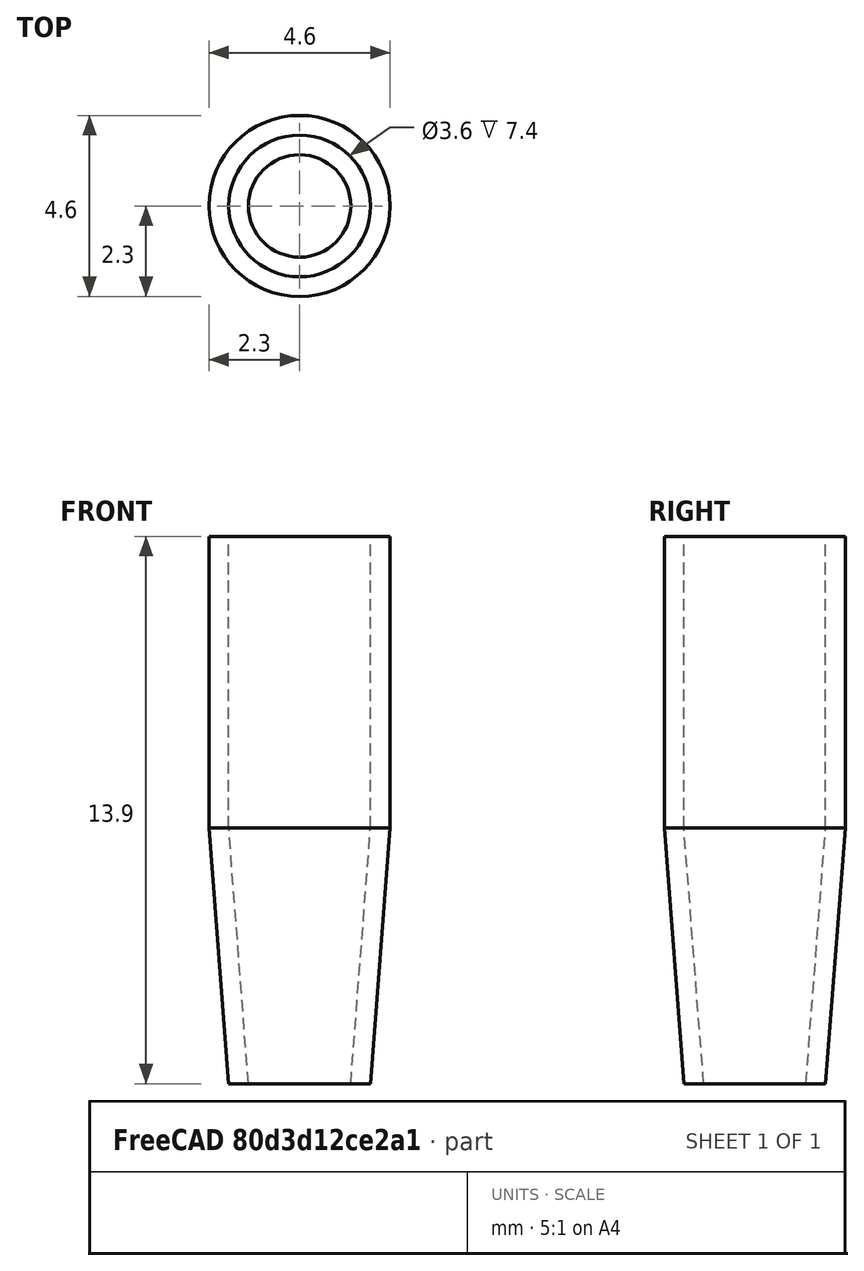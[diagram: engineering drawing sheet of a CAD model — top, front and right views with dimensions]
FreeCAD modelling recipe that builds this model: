
FCSTD DOCUMENT  (FreeCAD 0.18.4R)
Label: vtulka
License: All rights reserved
LicenseURL: http://en.wikipedia.org/wiki/All_rights_reserved
objects: Part::Cone×2, Part::Cylinder×2, Part::MultiFuse×2, Part::Cut×1, App::Part×1
note: 7 computed .brp shape members not serialized (recipe doc carries the construction recipe); baked Part::Feature solids carry a one-line shape summary decoded from their .brp

FEATURE [Part::Cone] Cone
  Angle = 360
  AttacherType = Attacher::AttachEngine3D
  Height = 6.5
  Placement = pos=(0,0,-6.5) rot=(0,0,1;0rad)
  Radius1 = 1.8
  Radius2 = 2.3
FEATURE [Part::Cylinder] Cylinder
  Angle = 360
  AttacherType = Attacher::AttachEngine3D
  Height = 7.4
  Radius = 2.3
FEATURE [Part::MultiFuse] Fusion  label="outer fusion"
  Shapes = -> [Cylinder,Cone]
FEATURE [Part::Cylinder] Cylinder001
  Angle = 360
  AttacherType = Attacher::AttachEngine3D
  Height = 7.4
  Radius = 1.8
FEATURE [Part::Cone] Cone001
  Angle = 360
  AttacherType = Attacher::AttachEngine3D
  Height = 6.5
  Placement = pos=(0,0,-6.5) rot=(0,0,1;0rad)
  Radius1 = 1.3
  Radius2 = 1.8
FEATURE [Part::MultiFuse] Fusion001  label="inner fusion"
  Shapes = -> [Cylinder001,Cone001]
FEATURE [Part::Cut] Cut  label="vtulka cut"
  Base = -> Fusion
  Tool = -> Fusion001
FEATURE [App::Part] Part  label="extruder vtulka"
  Group = -> [Cone001,Cylinder001,Fusion001,Cylinder,Cone,Fusion,Cut]
  Origin = -> Origin
